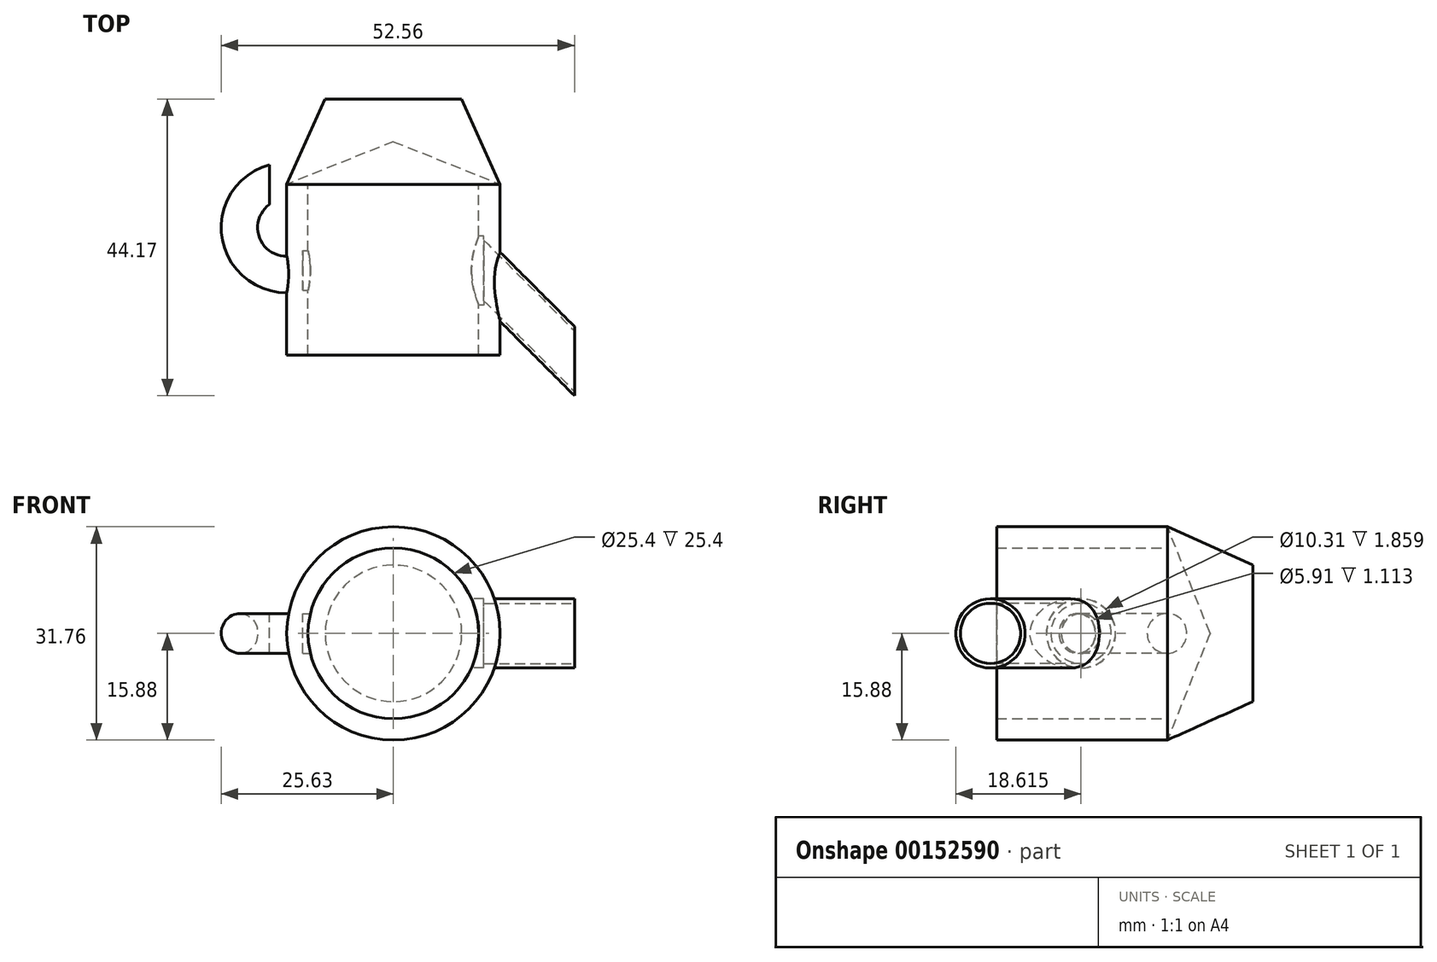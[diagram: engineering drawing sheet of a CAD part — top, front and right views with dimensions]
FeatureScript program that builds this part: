
annotation { "Feature Type Name" : "Feature", "Feature Type Description" : "" }
export const myFeature = defineFeature(function(context is Context, id is Id, definition is map)
    precondition{}
    {
        {
            var Q0;
            Q0=qCreatedBy(makeId("Front.planeOp"),FACE);
            var sketch = newSketch(context, id + "F0", { "sketchPlane" : qUnion([Q0])});
            skCircle(sketch, "E0", {"center": v(0, 0) * mm, "radius": 12.7 * mm});
            skCircle(sketch, "E1", {"center": v(0, 0) * mm, "radius": 15.88 * mm});
            skLineSegment(sketch, "E2", {"start": v(0, 0) * mm, "end": v(15.88, 0) * mm});
            skSolve(sketch);
        }
        {
            var Q0;
            Q0 = qSketchRegion(id + "F0", true);
            extrude(context, id + "F1", {"entities" : qUnion([Q0]), "depth" : 25.4 * mm});
        }
        {
            var Q0;
            Q0=qCreatedBy(makeId("Top.planeOp"),FACE);
            var sketch = newSketch(context, id + "F2", { "sketchPlane" : qUnion([Q0])});
            skLineSegment(sketch, "E3", {"start": v(0, 6.35) * mm, "end": v(0, 12.7) * mm});
            skLineSegment(sketch, "E4", {"start": v(0, 12.7) * mm, "end": v(10.16, 12.7) * mm});
            skLineSegment(sketch, "E5", {"start": v(10.16, 12.7) * mm, "end": v(15.88, 0) * mm});
            skLineSegment(sketch, "E6", {"start": v(0, 6.35) * mm, "end": v(15.88, 0) * mm});
            skPoint(sketch, "E7.orphan", {"position": v(0, 0) * mm});
            skSolve(sketch);
        }
        {
            var Q0;
            Q0=makeQuery(id+"F2.imprint","IMPRINT",FACE,{"disambiguationData":[TD([[makeQuery(id+"F2.imprint","IMPRINT",EDGE,{"derivedFrom":sQuery(id+"F2.wireOp",EDGE,"E3")}),-1.0]])]});
            var Q1;
            Q1=sQuery(id+"F2.wireOp",EDGE,"E3");
            revolve(context, id + "F3", {"entities" : qUnion([Q0]), "axis" : qUnion([Q1]), "revolveType" : RevolveType.FULL});
        }
        {
            var Q0;
            Q0=qCreatedBy(makeId("Right.planeOp"),FACE);
            var sketch = newSketch(context, id + "F4", { "sketchPlane" : qUnion([Q0])});
            skCircle(sketch, "E8", {"center": v(-12.85, 0) * mm, "radius": 5.16 * mm});
            skLineSegment(sketch, "E9", {"start": v(-12.85, 0) * mm, "end": v(0, 0) * mm});
            skCircle(sketch, "E10", {"center": v(-12.85, 0) * mm, "radius": 2.95 * mm});
            skSolve(sketch);
        }
        {
            var Q0;
            Q0=qCreatedBy(makeId("Top.planeOp"),FACE);
            var sketch = newSketch(context, id + "F5", { "sketchPlane" : qUnion([Q0])});
            skLineSegment(sketch, "E11", {"start": v(0, 0) * mm, "end": v(0, -12.9) * mm});
            skLineSegment(sketch, "E12.bottom", {"start": v(0, -12.9) * mm, "end": v(13.46, -12.9) * mm});
            skLineSegment(sketch, "E12.left", {"start": v(0, -12.9) * mm, "end": v(0, -26.37) * mm});
            skLineSegment(sketch, "E12.right", {"start": v(13.46, -12.9) * mm, "end": v(13.46, -26.37) * mm});
            skLineSegment(sketch, "E13", {"start": v(0, -12.9) * mm, "end": v(13.46, -26.37) * mm});
            skLineSegment(sketch, "E14.right", {"start": v(27.03, -12.86) * mm, "end": v(27.03, -26.32) * mm});
            skLineSegment(sketch, "E15", {"start": v(13.46, -12.9) * mm, "end": v(26.93, -26.37) * mm});
            skSolve(sketch);
        }
        {
            var Q0;
            Q0=makeQuery(id+"F4.imprint","IMPRINT",FACE,{"disambiguationData":[TD([[makeQuery(id+"F4.imprint","IMPRINT",EDGE,{"derivedFrom":sQuery(id+"F4.wireOp",EDGE,"E8")}),1.0]])]});
            var Q1;
            Q1=makeQuery(id+"F4.imprint","IMPRINT",FACE,{"disambiguationData":[TD([[makeQuery(id+"F4.imprint","IMPRINT",EDGE,{"derivedFrom":sQuery(id+"F4.wireOp",EDGE,"E10")}),1.0]])]});
            extrude(context, id + "F6", {"entities" : qUnion([Q0, Q1]), "operationType" : NewBodyOperationType.REMOVE, "depth" : 13.46 * mm});
        }
        {
            var Q0;
            Q0=makeQuery(id+"F6.boolean.opBoolean","COPY",FACE,{"derivedFrom":makeQuery(id+"F6.opExtrude","CAP_FACE",FACE,{"disambiguationData":[OSD([sQuery(id+"F4.wireOp",EDGE,"E8")])],"isStart":false})});
            var Q1;
            Q1=sQuery(id+"F5.wireOp",EDGE,"E15");
            sweep(context, id + "F7", {"operationType" : NewBodyOperationType.ADD, "profiles" : qUnion([Q0]), "path" : qUnion([Q1])});
        }
        {
            var Q0;
            Q0=makeQuery(id+"F7.opSweep","CAP_FACE",FACE,{"disambiguationData":[OSD([sQuery(id+"F4.wireOp",EDGE,"E8"),sQuery(id+"F5.wireOp",VERTEX,"E15.end")])],"isStart":false});
            var sketch = newSketch(context, id + "F8", { "sketchPlane" : qUnion([Q0])});
            skCircle(sketch, "E16", {"center": v(-26.32, 0) * mm, "radius": 4.5 * mm});
            skSolve(sketch);
        }
        {
            var Q0;
            Q0=makeQuery(id+"F8.imprint","IMPRINT",FACE,{"disambiguationData":[TD([[makeQuery(id+"F8.imprint","IMPRINT",EDGE,{"derivedFrom":sQuery(id+"F8.wireOp",EDGE,"E16")}),1.0]])]});
            var Q1;
            Q1=sQuery(id+"F5.wireOp",EDGE,"E15");
            sweep(context, id + "F9", {"operationType" : NewBodyOperationType.REMOVE, "profiles" : qUnion([Q0]), "path" : qUnion([Q1])});
        }
        {
            var Q0;
            Q0=qCreatedBy(makeId("Top.planeOp"),FACE);
            var sketch = newSketch(context, id + "F10", { "sketchPlane" : qUnion([Q0])});
            skLineSegment(sketch, "E17", {"start": v(0, 0) * mm, "end": v(-15.95, 0) * mm});
            skLineSegment(sketch, "E18", {"start": v(-15.95, 0) * mm, "end": v(-15.95, -14.93) * mm});
            skLineSegment(sketch, "E19", {"start": v(-15.95, 0) * mm, "end": v(-15.95, -12.9) * mm});
            skArc(sketch, "E20", {"start": v(-15.95, 0) * mm, "mid": v(-22.4, -6.45) * mm, "end": v(-15.95, -12.9) * mm});
            skSolve(sketch);
        }
        {
            var Q0;
            Q0=makeQuery(id+"F4.imprint","IMPRINT",FACE,{"disambiguationData":[TD([[makeQuery(id+"F4.imprint","IMPRINT",EDGE,{"derivedFrom":sQuery(id+"F4.wireOp",EDGE,"E10")}),1.0]])]});
            extrude(context, id + "F11", {"entities" : qUnion([Q0]), "operationType" : NewBodyOperationType.REMOVE, "oppositeDirection" : true, "depth" : 13.46 * mm});
        }
        {
            var Q0;
            Q0=makeQuery(id+"F11.boolean.opBoolean","COPY",FACE,{"derivedFrom":makeQuery(id+"F11.opExtrude","CAP_FACE",FACE,{"disambiguationData":[OSD([sQuery(id+"F4.wireOp",EDGE,"E10")])],"isStart":false})});
            var Q1;
            Q1=sQuery(id+"F10.wireOp",EDGE,"E20");
            sweep(context, id + "F12", {"operationType" : NewBodyOperationType.ADD, "profiles" : qUnion([Q0]), "path" : qUnion([Q1])});
        }
    });
